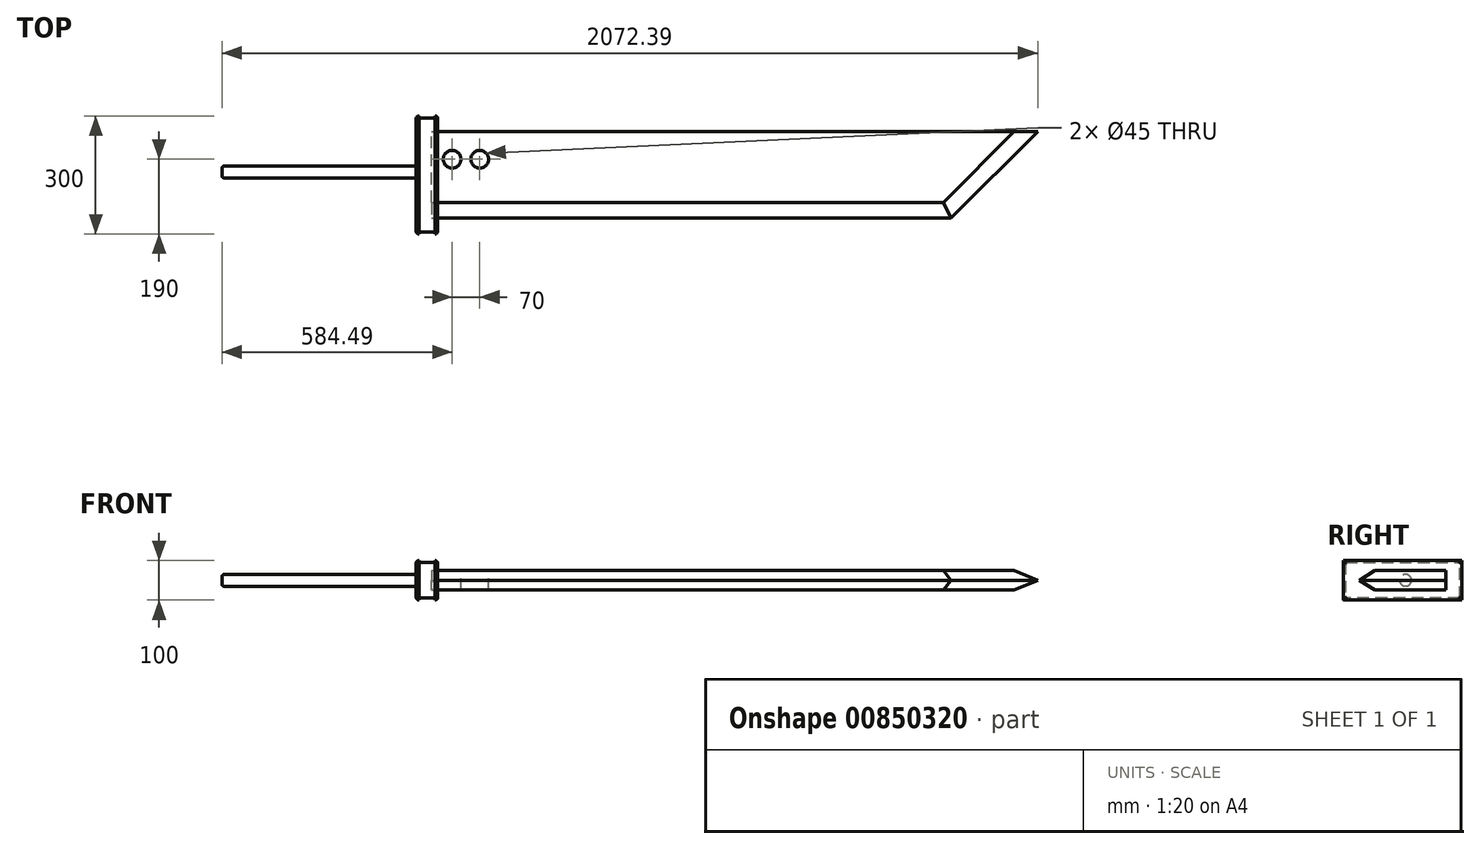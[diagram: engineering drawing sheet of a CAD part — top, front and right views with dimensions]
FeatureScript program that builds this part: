
annotation { "Feature Type Name" : "Feature", "Feature Type Description" : "" }
export const myFeature = defineFeature(function(context is Context, id is Id, definition is map)
    precondition{}
    {
        {
            var Q0;
            Q0=qCreatedBy(makeId("Top.planeOp"),FACE);
            var sketch = newSketch(context, id + "F0", { "sketchPlane" : qUnion([Q0])});
            skLineSegment(sketch, "E0", {"start": v(0, 0) * mm, "end": v(1600, 0) * mm});
            skLineSegment(sketch, "E1", {"start": v(1600, 0) * mm, "end": v(1300, -300) * mm});
            skLineSegment(sketch, "E2", {"start": v(1300, -300) * mm, "end": v(0, -300) * mm});
            skLineSegment(sketch, "E3", {"start": v(0, -300) * mm, "end": v(0, 0) * mm});
            skSolve(sketch);
        }
        {
            var Q0;
            Q0=makeQuery(id+"F0.imprint","IMPRINT",FACE,{"disambiguationData":[TD([[makeQuery(id+"F0.imprint","IMPRINT",EDGE,{"derivedFrom":sQuery(id+"F0.wireOp",EDGE,"E0")}),-1.0]])]});
            extrude(context, id + "F1", {"entities" : qUnion([Q0]), "depth" : 25 * mm, "offsetDistance" : 25 * mm});
        }
        {
            var Q0;
            Q0=makeQuery(id+"F1.opExtrude","CAP_EDGE",EDGE,{"disambiguationData":[OSD([sQuery(id+"F0.wireOp",EDGE,"E2")])],"isStart":false});
            chamfer(context, id + "F2", {"entities" : qUnion([Q0]), "chamferType" : ChamferType.TWO_OFFSETS, "width1" : 120 * mm, "oppositeDirection" : true, "width2" : 75 * mm, "tangentPropagation" : true});
        }
        {
            var Q0;
            Q0=makeQuery(id+"F1.opExtrude","CAP_EDGE",EDGE,{"disambiguationData":[OSD([sQuery(id+"F0.wireOp",EDGE,"E1")])],"isStart":false});
            chamfer(context, id + "F3", {"entities" : qUnion([Q0]), "chamferType" : ChamferType.TWO_OFFSETS, "width1" : 50 * mm, "oppositeDirection" : false, "width2" : 85 * mm, "tangentPropagation" : true});
        }
        {
            var Q0;
            Q0=makeQuery(id+"F1.opExtrude","SWEPT_BODY",BODY,{"disambiguationData":[OSD([sQuery(id+"F0.wireOp",EDGE,"E0"),sQuery(id+"F0.wireOp",EDGE,"E1"),sQuery(id+"F0.wireOp",EDGE,"E2"),sQuery(id+"F0.wireOp",EDGE,"E3")])]});
            var Q1;
            Q1=makeQuery(id+"F1.opExtrude","CAP_FACE",FACE,{"disambiguationData":[OSD([sQuery(id+"F0.wireOp",EDGE,"E0"),sQuery(id+"F0.wireOp",EDGE,"E1"),sQuery(id+"F0.wireOp",EDGE,"E2"),sQuery(id+"F0.wireOp",EDGE,"E3")])],"isStart":true});
            mirror(context, id + "F4", {"operationType" : NewBodyOperationType.ADD, "entities" : qUnion([Q0]), "mirrorPlane" : qUnion([Q1])});
        }
        {
            var Q0;
            Q0=makeQuery(id+"F1.opExtrude","CAP_FACE",FACE,{"disambiguationData":[OSD([sQuery(id+"F0.wireOp",EDGE,"E0"),sQuery(id+"F0.wireOp",EDGE,"E1"),sQuery(id+"F0.wireOp",EDGE,"E2"),sQuery(id+"F0.wireOp",EDGE,"E3")])],"isStart":false});
            var sketch = newSketch(context, id + "F5", { "sketchPlane" : qUnion([Q0])});
            skCircle(sketch, "E4", {"center": v(52, -70) * mm, "radius": 22.5 * mm});
            skCircle(sketch, "E5", {"center": v(122, -70) * mm, "radius": 22.5 * mm});
            skSolve(sketch);
        }
        {
            var Q0;
            Q0=makeQuery(id+"F5.imprint","IMPRINT",FACE,{"disambiguationData":[TD([[makeQuery(id+"F5.imprint","IMPRINT",EDGE,{"derivedFrom":sQuery(id+"F5.wireOp",EDGE,"E4")}),1.0]])]});
            var Q1;
            Q1=makeQuery(id+"F5.imprint","IMPRINT",FACE,{"disambiguationData":[TD([[makeQuery(id+"F5.imprint","IMPRINT",EDGE,{"derivedFrom":sQuery(id+"F5.wireOp",EDGE,"E5")}),1.0]])]});
            extrude(context, id + "F6", {"entities" : qUnion([Q0, Q1]), "operationType" : NewBodyOperationType.REMOVE, "oppositeDirection" : true, "depth" : 100 * mm, "offsetDistance" : 25 * mm});
        }
        {
            var Q0;
            Q0=qCreatedBy(makeId("Top.planeOp"),FACE);
            var sketch = newSketch(context, id + "F7", { "sketchPlane" : qUnion([Q0])});
            skLineSegment(sketch, "E6", {"start": v(15.5, 40) * mm, "end": v(-39.5, 40) * mm});
            skLineSegment(sketch, "E7", {"start": v(15.5, 40) * mm, "end": v(15.5, 40) * mm});
            skLineSegment(sketch, "E8", {"start": v(-39.5, 40) * mm, "end": v(-39.5, -260) * mm});
            skLineSegment(sketch, "E9", {"start": v(-39.5, -260) * mm, "end": v(15.5, -260) * mm});
            skLineSegment(sketch, "E10", {"start": v(15.5, -260) * mm, "end": v(15.5, -260) * mm});
            skLineSegment(sketch, "E11", {"start": v(15.5, -260) * mm, "end": v(15.5, 40) * mm});
            skSolve(sketch);
        }
        {
            var Q0;
            Q0=qSketchRegion(id+"F7",true);
            extrude(context, id + "F8", {"entities" : qUnion([Q0]), "endBound" : BoundingType.SYMMETRIC, "depth" : 100 * mm, "offsetDistance" : 25 * mm});
        }
        {
            var Q0;
            Q0=makeQuery(id+"F8.opExtrude","CAP_EDGE",EDGE,{"disambiguationData":[OSD([sQuery(id+"F7.wireOp",EDGE,"E7"),sQuery(id+"F7.wireOp",EDGE,"E10"),sQuery(id+"F7.wireOp",EDGE,"E11")])],"isStart":false});
            var Q1;
            Q1=makeQuery(id+"F8.opExtrude","CAP_EDGE",EDGE,{"disambiguationData":[OSD([sQuery(id+"F7.wireOp",EDGE,"E7"),sQuery(id+"F7.wireOp",EDGE,"E10"),sQuery(id+"F7.wireOp",EDGE,"E11")])],"isStart":true});
            var Q2;
            Q2=makeQuery(id+"F8.opExtrude","CAP_EDGE",EDGE,{"disambiguationData":[OSD([sQuery(id+"F7.wireOp",EDGE,"E8")])],"isStart":false});
            var Q3;
            Q3=makeQuery(id+"F8.opExtrude","SWEPT_EDGE",EDGE,{"disambiguationData":[OSD([sQuery(id+"F7.wireOp",EDGE,"E8"),sQuery(id+"F7.wireOp",EDGE,"E9")])]});
            var Q4;
            Q4=makeQuery(id+"F8.opExtrude","SWEPT_EDGE",EDGE,{"disambiguationData":[OSD([sQuery(id+"F7.wireOp",EDGE,"E9"),sQuery(id+"F7.wireOp",EDGE,"E10")])]});
            var Q5;
            Q5=makeQuery(id+"F8.opExtrude","CAP_EDGE",EDGE,{"disambiguationData":[OSD([sQuery(id+"F7.wireOp",EDGE,"E8")])],"isStart":true});
            var Q6;
            Q6=makeQuery(id+"F8.opExtrude","SWEPT_EDGE",EDGE,{"disambiguationData":[OSD([sQuery(id+"F7.wireOp",EDGE,"E6"),sQuery(id+"F7.wireOp",EDGE,"E8")])]});
            var Q7;
            Q7=makeQuery(id+"F8.opExtrude","SWEPT_EDGE",EDGE,{"disambiguationData":[OSD([sQuery(id+"F7.wireOp",EDGE,"E6"),sQuery(id+"F7.wireOp",EDGE,"E7")])]});
            fillet(context, id + "F9", {"entities" : qUnion([Q0, Q1, Q2, Q3, Q4, Q5, Q6, Q7]), "radius" : 7 * mm, "tangentPropagation" : true, "allowEdgeOverflow" : false});
        }
        {
            var Q0;
            Q0=makeQuery(id+"F8.opExtrude","CAP_FACE",FACE,{"disambiguationData":[OSD([sQuery(id+"F7.wireOp",EDGE,"E6"),sQuery(id+"F7.wireOp",EDGE,"E7"),sQuery(id+"F7.wireOp",EDGE,"E8"),sQuery(id+"F7.wireOp",EDGE,"E9"),sQuery(id+"F7.wireOp",EDGE,"E10"),sQuery(id+"F7.wireOp",EDGE,"E11")])],"isStart":false});
            extrude(context, id + "F10", {"entities" : qUnion([Q0]), "operationType" : NewBodyOperationType.REMOVE, "oppositeDirection" : true, "depth" : 5 * mm, "offsetDistance" : 25 * mm});
        }
        {
            var Q0;
            Q0=makeQuery(id+"F8.opExtrude","SWEPT_FACE",FACE,{"disambiguationData":[OSD([sQuery(id+"F7.wireOp",EDGE,"E9")])]});
            extrude(context, id + "F11", {"entities" : qUnion([Q0]), "operationType" : NewBodyOperationType.REMOVE, "oppositeDirection" : true, "depth" : 5 * mm, "offsetDistance" : 25 * mm});
        }
        {
            var Q0;
            Q0=makeQuery(id+"F8.opExtrude","CAP_FACE",FACE,{"disambiguationData":[OSD([sQuery(id+"F7.wireOp",EDGE,"E6"),sQuery(id+"F7.wireOp",EDGE,"E7"),sQuery(id+"F7.wireOp",EDGE,"E8"),sQuery(id+"F7.wireOp",EDGE,"E9"),sQuery(id+"F7.wireOp",EDGE,"E10"),sQuery(id+"F7.wireOp",EDGE,"E11")])],"isStart":true});
            extrude(context, id + "F12", {"entities" : qUnion([Q0]), "operationType" : NewBodyOperationType.REMOVE, "oppositeDirection" : true, "depth" : 5 * mm, "offsetDistance" : 25 * mm});
        }
        {
            var Q0;
            Q0=makeQuery(id+"F8.opExtrude","SWEPT_FACE",FACE,{"disambiguationData":[OSD([sQuery(id+"F7.wireOp",EDGE,"E6")])]});
            extrude(context, id + "F13", {"entities" : qUnion([Q0]), "operationType" : NewBodyOperationType.REMOVE, "oppositeDirection" : true, "depth" : 5 * mm, "offsetDistance" : 25 * mm});
        }
        {
            var Q0;
            {var subQ0=sQuery(id+"F7.wireOp",EDGE,"E9");Q0=makeQuery(id+"F11.boolean.opBoolean","COPY",EDGE,{"derivedFrom":makeQuery(id+"F11.opExtrude","CAP_EDGE",EDGE,{"disambiguationData":[OSD([subQ0]),TDD([makeQuery(id+"F10.boolean.opBoolean","COPY",EDGE,{"derivedFrom":makeQuery(id+"F10.opExtrude","CAP_EDGE",EDGE,{"disambiguationData":[OSD([subQ0])],"isStart":false})})])],"isStart":false})});}
            var Q1;
            Q1=makeQuery(id+"F12.boolean.opBoolean","COPY",EDGE,{"derivedFrom":makeQuery(id+"F12.opExtrude","CAP_EDGE",EDGE,{"disambiguationData":[OSD([sQuery(id+"F7.wireOp",EDGE,"E9")])],"isStart":false})});
            var Q2;
            {var subQ0=sQuery(id+"F7.wireOp",EDGE,"E6");Q2=makeQuery(id+"F13.boolean.opBoolean","COPY",EDGE,{"derivedFrom":makeQuery(id+"F13.opExtrude","CAP_EDGE",EDGE,{"disambiguationData":[OSD([subQ0]),TDD([makeQuery(id+"F12.boolean.opBoolean","COPY",EDGE,{"derivedFrom":makeQuery(id+"F12.opExtrude","CAP_EDGE",EDGE,{"disambiguationData":[OSD([subQ0])],"isStart":false})})])],"isStart":false})});}
            var Q3;
            {var subQ0=sQuery(id+"F7.wireOp",EDGE,"E6");Q3=makeQuery(id+"F13.boolean.opBoolean","COPY",EDGE,{"derivedFrom":makeQuery(id+"F13.opExtrude","CAP_EDGE",EDGE,{"disambiguationData":[OSD([subQ0]),TDD([makeQuery(id+"F10.boolean.opBoolean","COPY",EDGE,{"derivedFrom":makeQuery(id+"F10.opExtrude","CAP_EDGE",EDGE,{"disambiguationData":[OSD([subQ0])],"isStart":false})})])],"isStart":false})});}
            fillet(context, id + "F14", {"entities" : qUnion([Q0, Q1, Q2, Q3]), "radius" : 5 * mm, "tangentPropagation" : true, "allowEdgeOverflow" : false});
        }
        {
            var Q0;
            Q0=qCreatedBy(makeId("Top.planeOp"),FACE);
            var sketch = newSketch(context, id + "F15", { "sketchPlane" : qUnion([Q0])});
            skLineSegment(sketch, "E12", {"start": v(-32.5, -117.53) * mm, "end": v(-532.5, -117.53) * mm});
            skLineSegment(sketch, "E13", {"start": v(-532.5, -117.53) * mm, "end": v(-532.5, -102.53) * mm});
            skLineSegment(sketch, "E14", {"start": v(-532.5, -102.53) * mm, "end": v(-32.5, -102.53) * mm});
            skLineSegment(sketch, "E15", {"start": v(-32.5, -102.53) * mm, "end": v(-32.5, -117.53) * mm});
            skSolve(sketch);
        }
        {
            var Q0;
            Q0=makeQuery(id+"F15.imprint","IMPRINT",FACE,{"disambiguationData":[TD([[makeQuery(id+"F15.imprint","IMPRINT",EDGE,{"derivedFrom":sQuery(id+"F15.wireOp",EDGE,"E12")}),-1.0]])]});
            var Q1;
            Q1=sQuery(id+"F15.wireOp",EDGE,"E14");
            revolve(context, id + "F16", {"operationType" : NewBodyOperationType.ADD, "surfaceOperationType" : NewSurfaceOperationType.NEW, "entities" : qUnion([Q0]), "axis" : qUnion([Q1]), "revolveType" : RevolveType.FULL});
        }
        {
            var Q0;
            Q0=makeQuery(id+"F16.opRevolve","SWEPT_EDGE",EDGE,{"disambiguationData":[OSD([sQuery(id+"F15.wireOp",EDGE,"E12"),sQuery(id+"F15.wireOp",EDGE,"E13")])]});
            fillet(context, id + "F17", {"entities" : qUnion([Q0]), "radius" : 5 * mm, "tangentPropagation" : true, "allowEdgeOverflow" : false});
        }
        {
            var Q0;
            Q0=makeQuery(id+"F16.boolean.opBoolean","INTERSECT",EDGE,{"derivedFrom":[makeQuery(id+"F8.opExtrude","SWEPT_FACE",FACE,{"disambiguationData":[OSD([sQuery(id+"F7.wireOp",EDGE,"E8")])]}),makeQuery(id+"F16.opRevolve","SWEPT_FACE",FACE,{"disambiguationData":[OSD([sQuery(id+"F15.wireOp",EDGE,"E12")])]})]});
            fillet(context, id + "F18", {"entities" : qUnion([Q0]), "radius" : 5 * mm, "tangentPropagation" : true, "allowEdgeOverflow" : false});
        }
        {
            var Q0;
            Q0=makeQuery(id+"F1.opExtrude","SWEPT_BODY",BODY,{"disambiguationData":[OSD([sQuery(id+"F0.wireOp",EDGE,"E0"),sQuery(id+"F0.wireOp",EDGE,"E1"),sQuery(id+"F0.wireOp",EDGE,"E2"),sQuery(id+"F0.wireOp",EDGE,"E3")])]});
            var Q1;
            Q1=makeQuery(id+"F8.opExtrude","SWEPT_BODY",BODY,{"disambiguationData":[OSD([sQuery(id+"F7.wireOp",EDGE,"E6"),sQuery(id+"F7.wireOp",EDGE,"E7"),sQuery(id+"F7.wireOp",EDGE,"E8"),sQuery(id+"F7.wireOp",EDGE,"E9"),sQuery(id+"F7.wireOp",EDGE,"E10"),sQuery(id+"F7.wireOp",EDGE,"E11")])]});
            booleanBodies(context, id + "F19", {"operationType" : BooleanOperationType.SUBTRACTION, "tools" : qUnion([Q0]), "targets" : qUnion([Q1]), "keepTools" : true});
        }
    });
